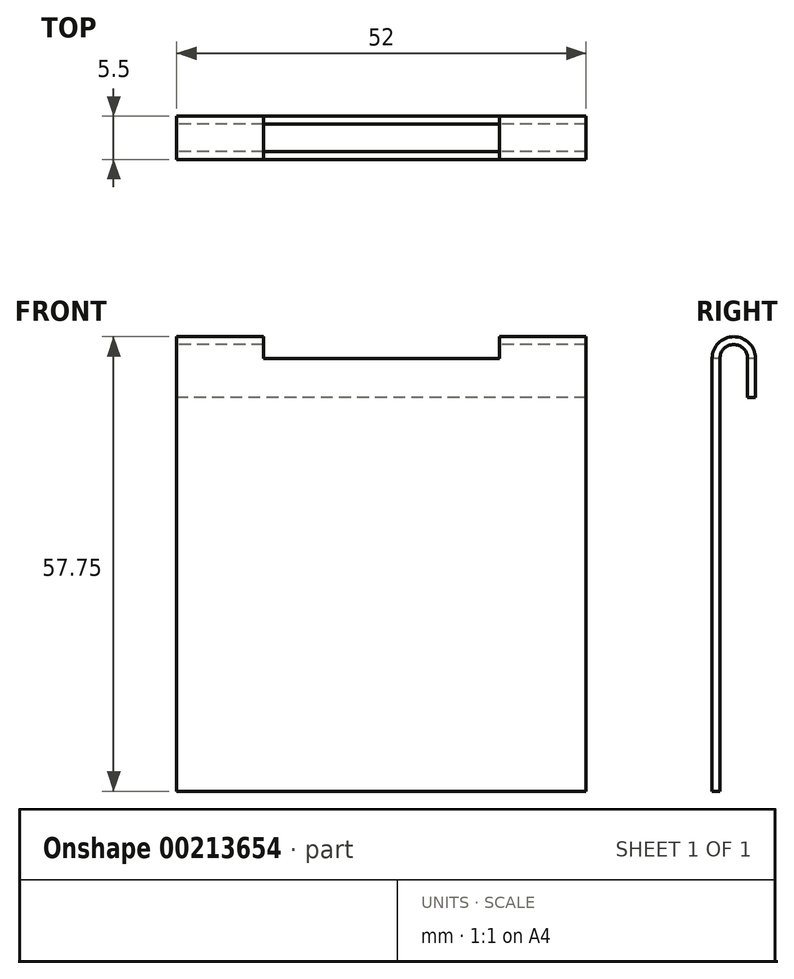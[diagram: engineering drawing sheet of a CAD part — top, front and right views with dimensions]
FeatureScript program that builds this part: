
annotation { "Feature Type Name" : "Feature", "Feature Type Description" : "" }
export const myFeature = defineFeature(function(context is Context, id is Id, definition is map)
    precondition{}
    {
        {
            var Q0;
            Q0=qCreatedBy(makeId("Right.planeOp"),FACE);
            var sketch = newSketch(context, id + "F0", { "sketchPlane" : qUnion([Q0])});
            skLineSegment(sketch, "E0", {"start": v(-1.75, 0) * mm, "end": v(-1.75, 55) * mm});
            skArc(sketch, "E1", {"start": v(-1.75, 55) * mm, "mid": v(0, 56.75) * mm, "end": v(1.75, 55) * mm});
            skLineSegment(sketch, "E2", {"start": v(1.75, 55) * mm, "end": v(1.75, 50) * mm});
            skLineSegment(sketch, "E3.0", {"start": v(2.75, 55) * mm, "end": v(2.75, 50) * mm});
            skArc(sketch, "E3.1", {"start": v(-2.75, 55) * mm, "mid": v(0, 57.75) * mm, "end": v(2.75, 55) * mm});
            skLineSegment(sketch, "E3.2", {"start": v(-2.75, 0) * mm, "end": v(-2.75, 55) * mm});
            skLineSegment(sketch, "E4", {"start": v(1.75, 50) * mm, "end": v(2.75, 50) * mm});
            skLineSegment(sketch, "E5", {"start": v(-2.75, 0) * mm, "end": v(-1.75, 0) * mm});
            skSolve(sketch);
        }
        {
            var Q0;
            Q0 = qSketchRegion(id + "F0", true);
            extrude(context, id + "F1", {"entities" : qUnion([Q0]), "endBound" : BoundingType.SYMMETRIC, "depth" : 52 * mm});
        }
        {
            var Q0;
            Q0=makeQuery(id+"F1.opExtrude","SWEPT_FACE",FACE,{"disambiguationData":[OSD([sQuery(id+"F0.wireOp",EDGE,"E3.2")])]});
            var sketch = newSketch(context, id + "F2", { "sketchPlane" : qUnion([Q0])});
            skLineSegment(sketch, "E6.bottom", {"start": v(15, 64) * mm, "end": v(-15, 64) * mm});
            skLineSegment(sketch, "E6.top", {"start": v(15, 54) * mm, "end": v(-15, 54) * mm});
            skLineSegment(sketch, "E6.left", {"start": v(15, 64) * mm, "end": v(15, 54) * mm});
            skLineSegment(sketch, "E6.right", {"start": v(-15, 64) * mm, "end": v(-15, 54) * mm});
            skPoint(sketch, "E6.middle", {"position": v(0, 59) * mm});
            skSolve(sketch);
        }
        {
            var Q0;
            {var subQ0=sQuery(id+"F2.wireOp",EDGE,"E6.bottom");Q0=makeQuery(id+"F2.imprint","IMPRINT",FACE,{"disambiguationData":[TD([[makeQuery(id+"F2.imprint","IMPRINT",EDGE,{"derivedFrom":subQ0}),1.0]])]});}
            extrude(context, id + "F3", {"entities" : qUnion([Q0]), "operationType" : NewBodyOperationType.REMOVE, "oppositeDirection" : true, "depth" : 25 * mm});
        }
    });
